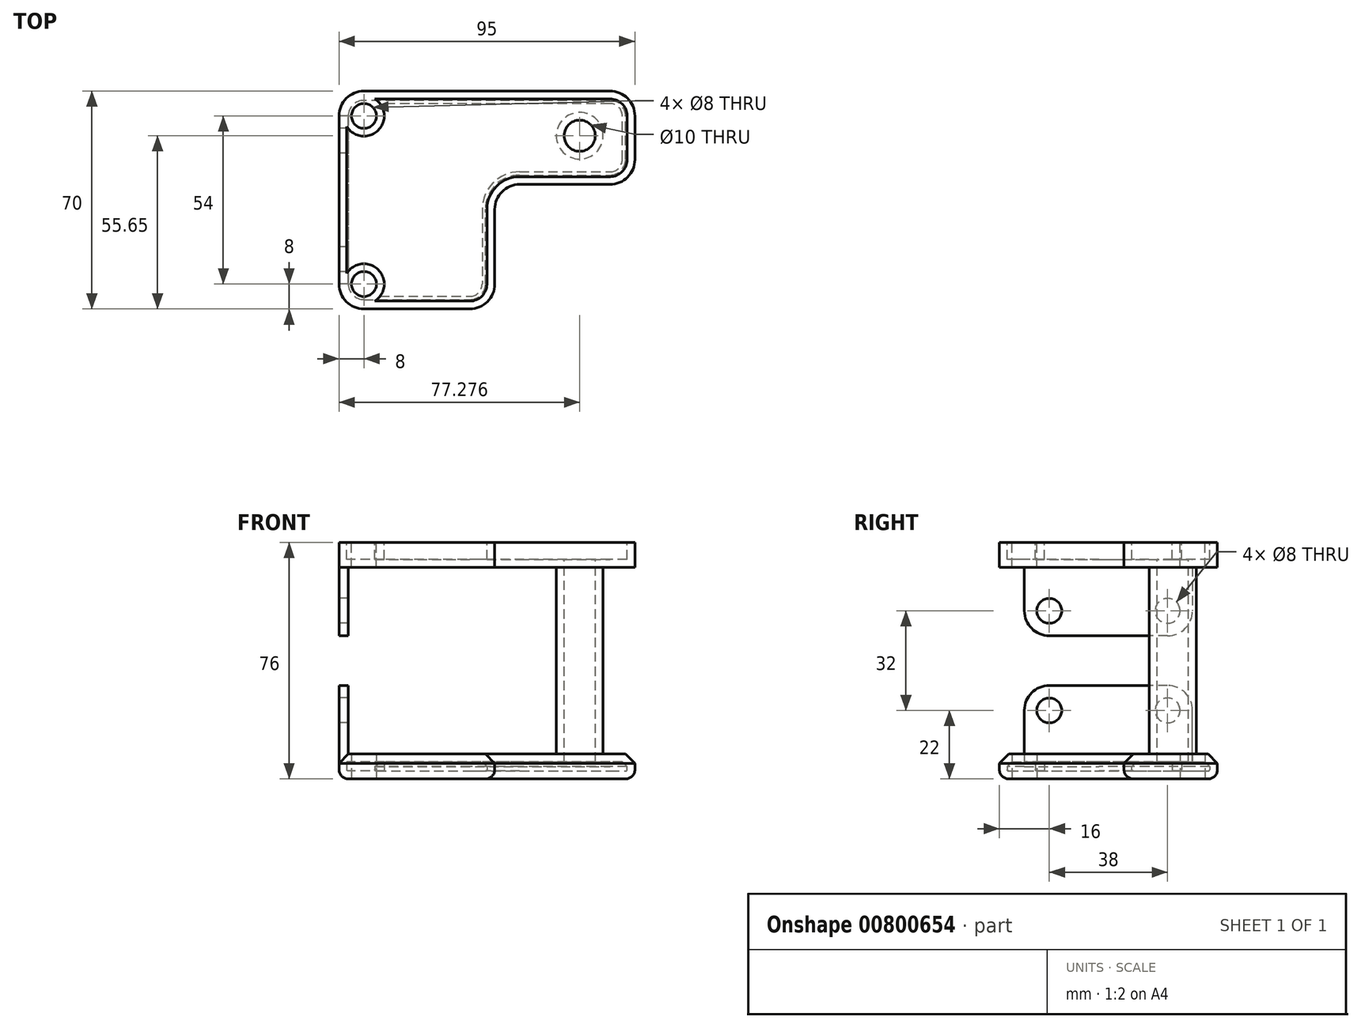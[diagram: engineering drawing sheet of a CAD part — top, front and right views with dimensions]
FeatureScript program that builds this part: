
annotation { "Feature Type Name" : "Feature", "Feature Type Description" : "" }
export const myFeature = defineFeature(function(context is Context, id is Id, definition is map)
    precondition{}
    {
        {
            var Q0;
            Q0=qCreatedBy(makeId("Top.planeOp"),FACE);
            var sketch = newSketch(context, id + "F0", { "sketchPlane" : qUnion([Q0])});
            skLineSegment(sketch, "E0", {"start": v(0, -8) * mm, "end": v(0, -32) * mm});
            skLineSegment(sketch, "E1", {"start": v(8, 0) * mm, "end": v(37, 0) * mm});
            skLineSegment(sketch, "E2", {"start": v(45, 8) * mm, "end": v(45, 22) * mm});
            skLineSegment(sketch, "E3", {"start": v(37, 30) * mm, "end": v(-42, 30) * mm});
            skLineSegment(sketch, "E4", {"start": v(-50, 22) * mm, "end": v(-50, -32) * mm});
            skLineSegment(sketch, "E5", {"start": v(-42, -40) * mm, "end": v(-8, -40) * mm});
            skPoint(sketch, "E6.visualSharp", {"position": v(45, 30) * mm});
            skArc(sketch, "E6.filletArc", {"start": v(45, 22) * mm, "mid": v(42.66, 27.66) * mm, "end": v(37, 30) * mm});
            skPoint(sketch, "E7.visualSharp", {"position": v(-50, 30) * mm});
            skArc(sketch, "E7.filletArc", {"start": v(-42, 30) * mm, "mid": v(-47.66, 27.66) * mm, "end": v(-50, 22) * mm});
            skPoint(sketch, "E8.visualSharp", {"position": v(-50, -40) * mm});
            skArc(sketch, "E8.filletArc", {"start": v(-50, -32) * mm, "mid": v(-47.66, -37.66) * mm, "end": v(-42, -40) * mm});
            skPoint(sketch, "E9.visualSharp", {"position": v(0, -40) * mm});
            skArc(sketch, "E9.filletArc", {"start": v(-8, -40) * mm, "mid": v(-2.34, -37.66) * mm, "end": v(0, -32) * mm});
            skPoint(sketch, "E10.visualSharp", {"position": v(0, 0) * mm});
            skArc(sketch, "E10.filletArc", {"start": v(8, 0) * mm, "mid": v(2.34, -2.34) * mm, "end": v(0, -8) * mm});
            skPoint(sketch, "E11.visualSharp", {"position": v(45, 0) * mm});
            skArc(sketch, "E11.filletArc", {"start": v(37, 0) * mm, "mid": v(42.66, 2.34) * mm, "end": v(45, 8) * mm});
            skCircle(sketch, "E12", {"center": v(-42, 22) * mm, "radius": 4 * mm});
            skCircle(sketch, "E13", {"center": v(-42, -32) * mm, "radius": 4 * mm});
            skSolve(sketch);
        }
        {
            var Q0;
            Q0=makeQuery(id+"F0.imprint","IMPRINT",FACE,{"disambiguationData":[TD([[makeQuery(id+"F0.imprint","IMPRINT",EDGE,{"derivedFrom":sQuery(id+"F0.wireOp",EDGE,"E0")}),-1.0]])]});
            extrude(context, id + "F1", {"entities" : qUnion([Q0]), "depth" : 8 * mm, "offsetDistance" : 25 * mm});
        }
        {
            var Q0;
            Q0=makeQuery(id+"F1.opExtrude","SWEPT_FACE",FACE,{"disambiguationData":[OSD([sQuery(id+"F0.wireOp",EDGE,"E4")])]});
            var sketch = newSketch(context, id + "F2", { "sketchPlane" : qUnion([Q0])});
            skLineSegment(sketch, "E14.bottom", {"start": v(-22, 0) * mm, "end": v(32, 0) * mm});
            skLineSegment(sketch, "E14.top", {"start": v(-14, 30) * mm, "end": v(24, 30) * mm});
            skLineSegment(sketch, "E14.left", {"start": v(-22, 0) * mm, "end": v(-22, 22) * mm});
            skLineSegment(sketch, "E14.right", {"start": v(32, 0) * mm, "end": v(32, 22) * mm});
            skPoint(sketch, "E15.visualSharp", {"position": v(-22, 30) * mm});
            skArc(sketch, "E15.filletArc", {"start": v(-14, 30) * mm, "mid": v(-19.66, 27.66) * mm, "end": v(-22, 22) * mm});
            skPoint(sketch, "E16.visualSharp", {"position": v(32, 30) * mm});
            skArc(sketch, "E16.filletArc", {"start": v(32, 22) * mm, "mid": v(29.66, 27.66) * mm, "end": v(24, 30) * mm});
            skCircle(sketch, "E17", {"center": v(24, 22) * mm, "radius": 4 * mm});
            skCircle(sketch, "E18", {"center": v(-14, 22) * mm, "radius": 4 * mm});
            skSolve(sketch);
        }
        {
            var Q0;
            {var subQ0=sQuery(id+"F2.wireOp",EDGE,"E14.top");Q0=makeQuery(id+"F2.imprint","IMPRINT",FACE,{"disambiguationData":[TD([[makeQuery(id+"F2.imprint","IMPRINT",EDGE,{"derivedFrom":subQ0}),-1.0]])]});}
            extrude(context, id + "F3", {"entities" : qUnion([Q0]), "operationType" : NewBodyOperationType.ADD, "oppositeDirection" : true, "depth" : 3 * mm, "offsetDistance" : 25 * mm});
        }
        {
            var Q0;
            Q0=makeQuery(id+"F1.opExtrude","CAP_FACE",FACE,{"disambiguationData":[OSD([sQuery(id+"F0.wireOp",EDGE,"E0"),sQuery(id+"F0.wireOp",EDGE,"E1"),sQuery(id+"F0.wireOp",EDGE,"E2"),sQuery(id+"F0.wireOp",EDGE,"E3"),sQuery(id+"F0.wireOp",EDGE,"E4"),sQuery(id+"F0.wireOp",EDGE,"E5"),sQuery(id+"F0.wireOp",EDGE,"E6.filletArc"),sQuery(id+"F0.wireOp",EDGE,"E7.filletArc"),sQuery(id+"F0.wireOp",EDGE,"E8.filletArc"),sQuery(id+"F0.wireOp",EDGE,"E9.filletArc"),sQuery(id+"F0.wireOp",EDGE,"E10.filletArc"),sQuery(id+"F0.wireOp",EDGE,"E11.filletArc"),sQuery(id+"F0.wireOp",EDGE,"E12"),sQuery(id+"F0.wireOp",EDGE,"E13")])],"isStart":false});
            cPlane(context, id + "F4", {"entities" : qUnion([Q0]), "cplaneType" : CPlaneType.OFFSET, "offset" : 60 * mm, "width" : 150 * mm, "height" : 150 * mm});
        }
        {
            var Q0;
            Q0=qCreatedBy(id+"F4.planeOp",FACE);
            var sketch = newSketch(context, id + "F5", { "sketchPlane" : qUnion([Q0])});
            skCircle(sketch, "E19", {"center": v(27.28, 15.65) * mm, "radius": 7.5 * mm});
            skSolve(sketch);
        }
        {
            var Q0;
            Q0=makeQuery(id+"F5.imprint","IMPRINT",FACE,{"disambiguationData":[TD([[makeQuery(id+"F5.imprint","IMPRINT",EDGE,{"derivedFrom":sQuery(id+"F5.wireOp",EDGE,"E19")}),1.0]])]});
            extrude(context, id + "F6", {"entities" : qUnion([Q0]), "endBound" : BoundingType.UP_TO_NEXT, "oppositeDirection" : true, "depth" : 25 * mm, "offsetDistance" : 25 * mm});
        }
        {
            var Q0;
            Q0=makeQuery(id+"F1.opExtrude","CAP_FACE",FACE,{"disambiguationData":[OSD([sQuery(id+"F0.wireOp",EDGE,"E0"),sQuery(id+"F0.wireOp",EDGE,"E1"),sQuery(id+"F0.wireOp",EDGE,"E2"),sQuery(id+"F0.wireOp",EDGE,"E3"),sQuery(id+"F0.wireOp",EDGE,"E4"),sQuery(id+"F0.wireOp",EDGE,"E5"),sQuery(id+"F0.wireOp",EDGE,"E6.filletArc"),sQuery(id+"F0.wireOp",EDGE,"E7.filletArc"),sQuery(id+"F0.wireOp",EDGE,"E8.filletArc"),sQuery(id+"F0.wireOp",EDGE,"E9.filletArc"),sQuery(id+"F0.wireOp",EDGE,"E10.filletArc"),sQuery(id+"F0.wireOp",EDGE,"E11.filletArc"),sQuery(id+"F0.wireOp",EDGE,"E12"),sQuery(id+"F0.wireOp",EDGE,"E13")])],"isStart":false});
            cPlane(context, id + "F7", {"entities" : qUnion([Q0]), "cplaneType" : CPlaneType.OFFSET, "offset" : 30 * mm, "width" : 150 * mm, "height" : 150 * mm});
        }
        {
            var Q0;
            Q0=makeQuery(id+"F1.opExtrude","SWEPT_BODY",BODY,{"disambiguationData":[OSD([sQuery(id+"F0.wireOp",EDGE,"E0"),sQuery(id+"F0.wireOp",EDGE,"E1"),sQuery(id+"F0.wireOp",EDGE,"E2"),sQuery(id+"F0.wireOp",EDGE,"E3"),sQuery(id+"F0.wireOp",EDGE,"E4"),sQuery(id+"F0.wireOp",EDGE,"E5"),sQuery(id+"F0.wireOp",EDGE,"E6.filletArc"),sQuery(id+"F0.wireOp",EDGE,"E7.filletArc"),sQuery(id+"F0.wireOp",EDGE,"E8.filletArc"),sQuery(id+"F0.wireOp",EDGE,"E9.filletArc"),sQuery(id+"F0.wireOp",EDGE,"E10.filletArc"),sQuery(id+"F0.wireOp",EDGE,"E11.filletArc"),sQuery(id+"F0.wireOp",EDGE,"E12"),sQuery(id+"F0.wireOp",EDGE,"E13")])]});
            var Q1;
            Q1=qCreatedBy(id+"F7.planeOp",FACE);
            mirror(context, id + "F8", {"operationType" : NewBodyOperationType.ADD, "entities" : qUnion([Q0]), "mirrorPlane" : qUnion([Q1])});
        }
        {
            var Q0;
            Q0=makeQuery(id+"F1.opExtrude","CAP_EDGE",EDGE,{"disambiguationData":[OSD([sQuery(id+"F0.wireOp",EDGE,"E5")])],"isStart":true});
            fillet(context, id + "F9", {"entities" : qUnion([Q0]), "radius" : 3 * mm, "tangentPropagation" : true, "allowEdgeOverflow" : false});
        }
        {
            var Q0;
            Q0=makeQuery(id+"F1.opExtrude","CAP_EDGE",EDGE,{"disambiguationData":[OSD([sQuery(id+"F0.wireOp",EDGE,"E5")])],"isStart":false});
            var Q1;
            Q1=makeQuery(id+"F1.opExtrude","CAP_EDGE",EDGE,{"disambiguationData":[OSD([sQuery(id+"F0.wireOp",EDGE,"E9.filletArc")])],"isStart":false});
            var Q2;
            Q2=makeQuery(id+"F1.opExtrude","CAP_EDGE",EDGE,{"disambiguationData":[OSD([sQuery(id+"F0.wireOp",EDGE,"E0")])],"isStart":false});
            chamfer(context, id + "F10", {"entities" : qUnion([Q0, Q1, Q2]), "width" : 3 * mm, "tangentPropagation" : true});
        }
        {
            var Q0;
            Q0=makeQuery(id+"F8.opPattern","COPY",FACE,{"derivedFrom":makeQuery(id+"F1.opExtrude","CAP_FACE",FACE,{"disambiguationData":[OSD([sQuery(id+"F0.wireOp",EDGE,"E0"),sQuery(id+"F0.wireOp",EDGE,"E1"),sQuery(id+"F0.wireOp",EDGE,"E2"),sQuery(id+"F0.wireOp",EDGE,"E3"),sQuery(id+"F0.wireOp",EDGE,"E4"),sQuery(id+"F0.wireOp",EDGE,"E5"),sQuery(id+"F0.wireOp",EDGE,"E6.filletArc"),sQuery(id+"F0.wireOp",EDGE,"E7.filletArc"),sQuery(id+"F0.wireOp",EDGE,"E8.filletArc"),sQuery(id+"F0.wireOp",EDGE,"E9.filletArc"),sQuery(id+"F0.wireOp",EDGE,"E10.filletArc"),sQuery(id+"F0.wireOp",EDGE,"E11.filletArc"),sQuery(id+"F0.wireOp",EDGE,"E12"),sQuery(id+"F0.wireOp",EDGE,"E13")])],"isStart":true}),"instanceName":"1"});
            shell(context, id + "F11", {"entities" : qUnion([Q0]), "thickness" : 2.5 * mm});
        }
    });
